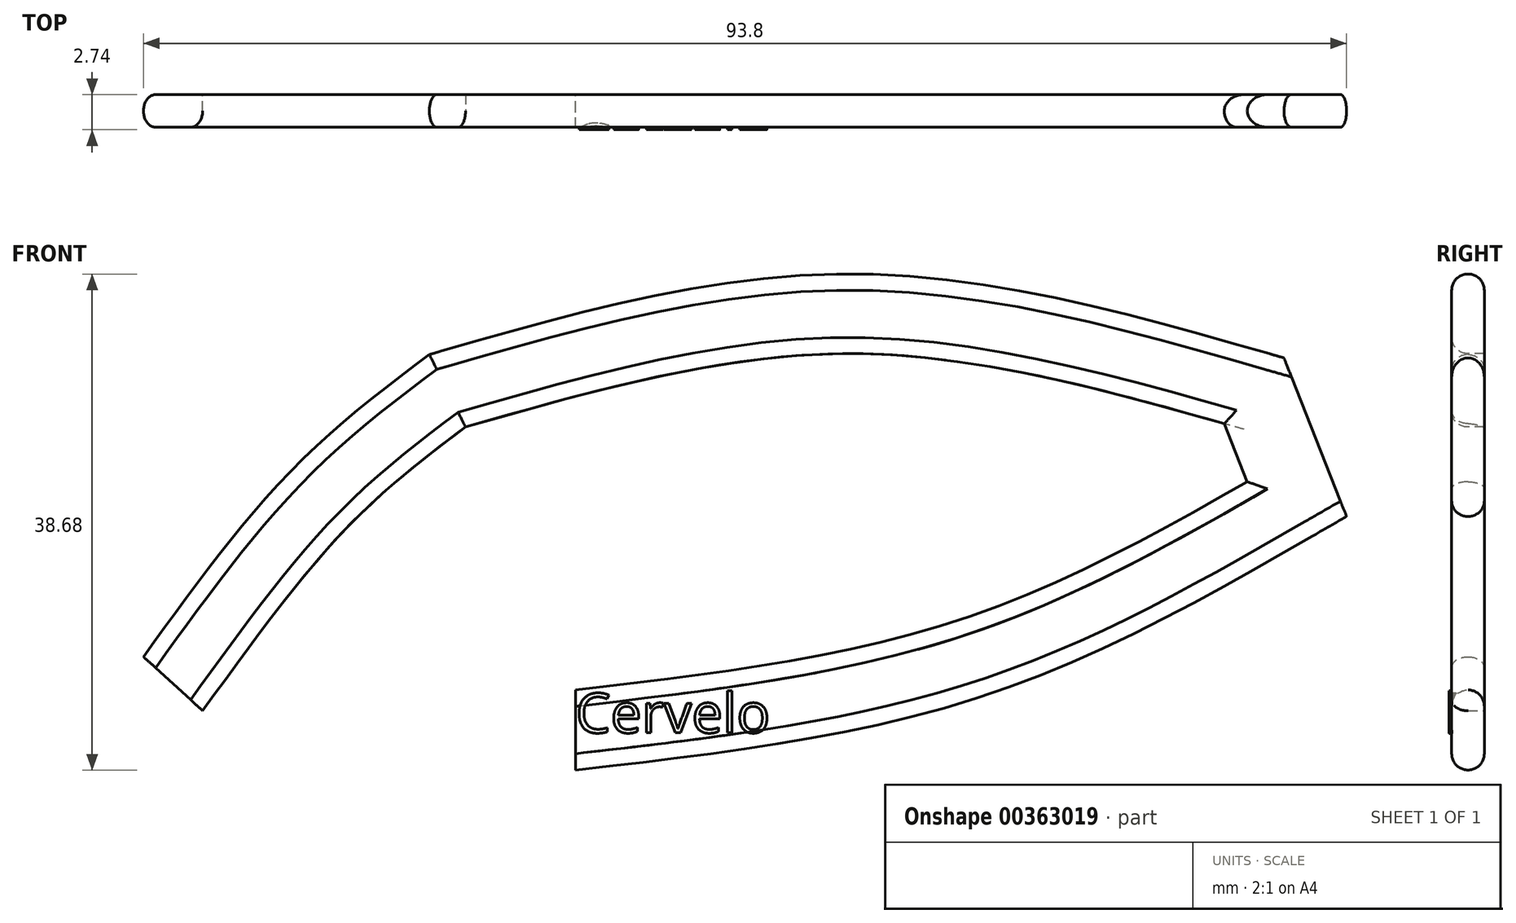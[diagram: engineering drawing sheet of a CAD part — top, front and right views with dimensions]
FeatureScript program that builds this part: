
annotation { "Feature Type Name" : "Feature", "Feature Type Description" : "" }
export const myFeature = defineFeature(function(context is Context, id is Id, definition is map)
    precondition{}
    {
        {
            var Q0;
            Q0=qCreatedBy(makeId("Right.planeOp"),FACE);
            var sketch = newSketch(context, id + "F0", { "sketchPlane" : qUnion([Q0])});
            skLineSegment(sketch, "E0.bottom", {"start": v(-1.27, 3.13) * mm, "end": v(1.27, 3.13) * mm});
            skLineSegment(sketch, "E0.top", {"start": v(-1.27, -3.13) * mm, "end": v(1.27, -3.13) * mm});
            skLineSegment(sketch, "E0.left", {"start": v(-1.27, 3.13) * mm, "end": v(-1.27, -3.13) * mm});
            skLineSegment(sketch, "E0.right", {"start": v(1.27, 3.13) * mm, "end": v(1.27, -3.13) * mm});
            skPoint(sketch, "E0.middle", {"position": v(0, 0) * mm});
            skSolve(sketch);
        }
        {
            var Q0;
            Q0=qCreatedBy(makeId("Front.planeOp"),FACE);
            var sketch = newSketch(context, id + "F1", { "sketchPlane" : qUnion([Q0])});
            skFitSpline(sketch, "E1", {"points": [v(0, 0) * mm, v(30.67, 5.56) * mm, v(56.23, 18) * mm], "startDerivative": vector(61.91, 7.12) * mm, "endDerivative": vector(50.46, 29.05) * mm});
            skLineSegment(sketch, "E2", {"start": v(56.23, 18) * mm, "end": v(52.9, 26.45) * mm});
            skFitSpline(sketch, "E3", {"points": [v(52.9, 26.45) * mm, v(21.34, 32.45) * mm, v(-10, 26.45) * mm], "startDerivative": vector(-63.07, 18) * mm, "endDerivative": vector(-62.72, -18.01) * mm});
            skFitSpline(sketch, "E4", {"points": [v(-1.9, 0) * mm, v(0.43, 29.44) * mm], "startDerivative": vector(2.34, 29.44) * mm, "endDerivative": vector(2.34, 29.44) * mm});
            skPoint(sketch, "E5.2.internal.orphan", {"position": v(-20, 18) * mm});
            skFitSpline(sketch, "E6", {"points": [v(-10, 26.45) * mm, v(-20, 18) * mm, v(-31.4, 3.6) * mm], "startDerivative": vector(-22.04, -16.6) * mm, "endDerivative": vector(-20.78, -28.76) * mm});
            skLineSegment(sketch, "E7", {"start": v(0.43, 29.44) * mm, "end": v(-1.9, 0) * mm});
            skSolve(sketch);
        }
        {
            var Q0;
            Q0=makeQuery(id+"F0.imprint","IMPRINT",FACE,{"disambiguationData":[TD([[makeQuery(id+"F0.imprint","IMPRINT",EDGE,{"derivedFrom":sQuery(id+"F0.wireOp",EDGE,"E0.bottom")}),-1.0]])]});
            var Q1;
            Q1=sQuery(id+"F1.wireOp",EDGE,"E1");
            var Q2;
            Q2=sQuery(id+"F1.wireOp",EDGE,"E2");
            var Q3;
            Q3=sQuery(id+"F1.wireOp",EDGE,"E3");
            var Q4;
            Q4=sQuery(id+"F1.wireOp",EDGE,"E6");
            sweep(context, id + "F2", {"profiles" : qUnion([Q0]), "path" : qUnion([Q1, Q2, Q3, Q4])});
        }
        {
            var Q0;
            Q0=makeQuery(id+"F2.opSweep","SWEPT_EDGE",EDGE,{"disambiguationData":[OSD([sQuery(id+"F0.wireOp",EDGE,"E0.top"),sQuery(id+"F0.wireOp",EDGE,"E0.left"),sQuery(id+"F1.wireOp",EDGE,"E3")]),OD(2.0)]});
            var Q1;
            Q1=makeQuery(id+"F2.opSweep","SWEPT_EDGE",EDGE,{"disambiguationData":[OSD([sQuery(id+"F0.wireOp",EDGE,"E0.top"),sQuery(id+"F0.wireOp",EDGE,"E0.right"),sQuery(id+"F1.wireOp",EDGE,"E3")]),OD(2.0)]});
            var Q2;
            Q2=makeQuery(id+"F2.opSweep","SWEPT_EDGE",EDGE,{"disambiguationData":[OSD([sQuery(id+"F0.wireOp",EDGE,"E0.top"),sQuery(id+"F0.wireOp",EDGE,"E0.right"),sQuery(id+"F1.wireOp",EDGE,"E6")]),OD(0.0)]});
            var Q3;
            Q3=makeQuery(id+"F2.opSweep","SWEPT_EDGE",EDGE,{"disambiguationData":[OSD([sQuery(id+"F0.wireOp",EDGE,"E0.top"),sQuery(id+"F0.wireOp",EDGE,"E0.left"),sQuery(id+"F1.wireOp",EDGE,"E6")]),OD(0.0)]});
            var Q4;
            Q4=makeQuery(id+"F2.opSweep","SWEPT_EDGE",EDGE,{"disambiguationData":[OSD([sQuery(id+"F0.wireOp",EDGE,"E0.bottom"),sQuery(id+"F0.wireOp",EDGE,"E0.left"),sQuery(id+"F1.wireOp",EDGE,"E6")])]});
            var Q5;
            Q5=makeQuery(id+"F2.opSweep","SWEPT_EDGE",EDGE,{"disambiguationData":[OSD([sQuery(id+"F0.wireOp",EDGE,"E0.bottom"),sQuery(id+"F0.wireOp",EDGE,"E0.left"),sQuery(id+"F1.wireOp",EDGE,"E3")])]});
            var Q6;
            Q6=makeQuery(id+"F2.opSweep","SWEPT_EDGE",EDGE,{"disambiguationData":[OSD([sQuery(id+"F0.wireOp",EDGE,"E0.top"),sQuery(id+"F0.wireOp",EDGE,"E0.left"),sQuery(id+"F1.wireOp",EDGE,"E1")]),OD(0.0)]});
            var Q7;
            Q7=makeQuery(id+"F2.opSweep","SWEPT_EDGE",EDGE,{"disambiguationData":[OSD([sQuery(id+"F0.wireOp",EDGE,"E0.top"),sQuery(id+"F0.wireOp",EDGE,"E0.right"),sQuery(id+"F1.wireOp",EDGE,"E1")]),OD(0.0)]});
            var Q8;
            Q8=makeQuery(id+"F2.opSweep","SWEPT_EDGE",EDGE,{"disambiguationData":[OSD([sQuery(id+"F0.wireOp",EDGE,"E0.bottom"),sQuery(id+"F0.wireOp",EDGE,"E0.right"),sQuery(id+"F1.wireOp",EDGE,"E1")])]});
            var Q9;
            Q9=makeQuery(id+"F2.opSweep","SWEPT_EDGE",EDGE,{"disambiguationData":[OSD([sQuery(id+"F0.wireOp",EDGE,"E0.bottom"),sQuery(id+"F0.wireOp",EDGE,"E0.left"),sQuery(id+"F1.wireOp",EDGE,"E1")])]});
            var Q10;
            Q10=makeQuery(id+"F2.opSweep","SWEPT_EDGE",EDGE,{"disambiguationData":[OSD([sQuery(id+"F0.wireOp",EDGE,"E0.bottom"),sQuery(id+"F0.wireOp",EDGE,"E0.left"),sQuery(id+"F1.wireOp",EDGE,"E2")])]});
            var Q11;
            Q11=makeQuery(id+"F2.opSweep","SWEPT_EDGE",EDGE,{"disambiguationData":[OSD([sQuery(id+"F0.wireOp",EDGE,"E0.bottom"),sQuery(id+"F0.wireOp",EDGE,"E0.right"),sQuery(id+"F1.wireOp",EDGE,"E2")])]});
            fillet(context, id + "F3", {"entities" : qUnion([Q0, Q1, Q2, Q3, Q4, Q5, Q6, Q7, Q8, Q9, Q10, Q11]), "radius" : 1.27 * mm, "tangentPropagation" : true, "allowEdgeOverflow" : false});
        }
        {
            var Q0;
            Q0=qCreatedBy(makeId("Front.planeOp"),FACE);
            var sketch = newSketch(context, id + "F4", { "sketchPlane" : qUnion([Q0])});
            skText(sketch, "E8", { "text": "Cervelo", "fontName": "OpenSans-Regular.ttf"});
            const initialGuessF4  = {"E8": [0, -0.00022, 1, 0, 0.0031]};
            skSetInitialGuess(sketch, initialGuessF4);
            skSolve(sketch);
        }
        {
            var Q0;
            Q0 = qSketchRegion(id + "F4", true);
            extrude(context, id + "F5", {"entities" : qUnion([Q0]), "operationType" : NewBodyOperationType.ADD, "depth" : 1.47 * mm});
        }
    });
